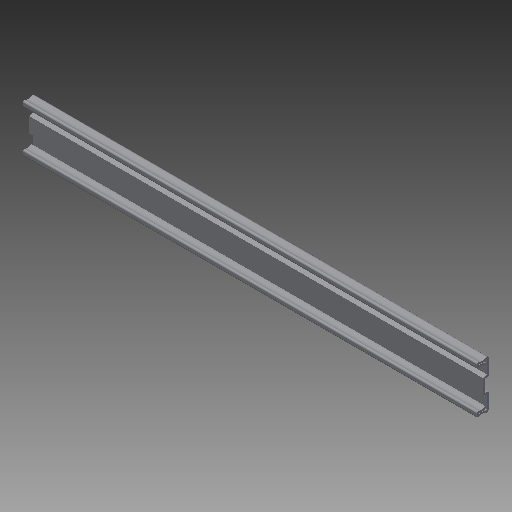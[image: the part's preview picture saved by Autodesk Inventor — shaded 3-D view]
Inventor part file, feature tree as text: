
AUTODESK INVENTOR PART (.ipt)
format: ipt  version: 2017 (Build 210142000, 142)  size: 207,872 bytes
history: native  units: in
note: dims shown in document units (in); Inventor stores cm internally (conversion verified against a paired STEP export)
features: extrude x1, other x1, imported_body x1
ambient origin geometry x8: Origin, YZ Plane, XZ Plane, XY Plane, X Axis, Y Axis, Z Axis, Center Point
bodies: Body1 (feature_tree)
feature tree (3):
  extrude  "Extrude3"  [1 undecoded]
  other  "63835A4201"
  imported_body  "Base1"
note: 1 required parameter value undecoded (feature->parameter linkage not recoverable at this tier; creation-order binding heuristic only, values carry confidence <= 0.55)
